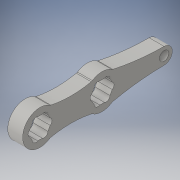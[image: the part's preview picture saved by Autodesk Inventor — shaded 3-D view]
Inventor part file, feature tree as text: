
AUTODESK INVENTOR PART (.ipt)
format: ipt  version: 2016 (Build 200138000, 138)  size: 161,280 bytes
history: native  units: in
note: dims shown in document units (in); Inventor stores cm internally (conversion verified against a paired STEP export)
features: extrude x1, sketch x1
ambient origin geometry x8: Origin, YZ Plane, XZ Plane, XY Plane, X Axis, Y Axis, Z Axis, Center Point
bodies: Solid1 (feature_tree)
feature tree (2):
  extrude  "Extrusion1"  Depth=0.6in
  sketch  "Sketch1"  dims[d0=1.4in d18=1.4in d21=0.66in d34=0.3752in d35=4.0in d36=4.0in d37=10.0in d38=10.0in d39=0.125in d40=0.6in d41=0.0in]
